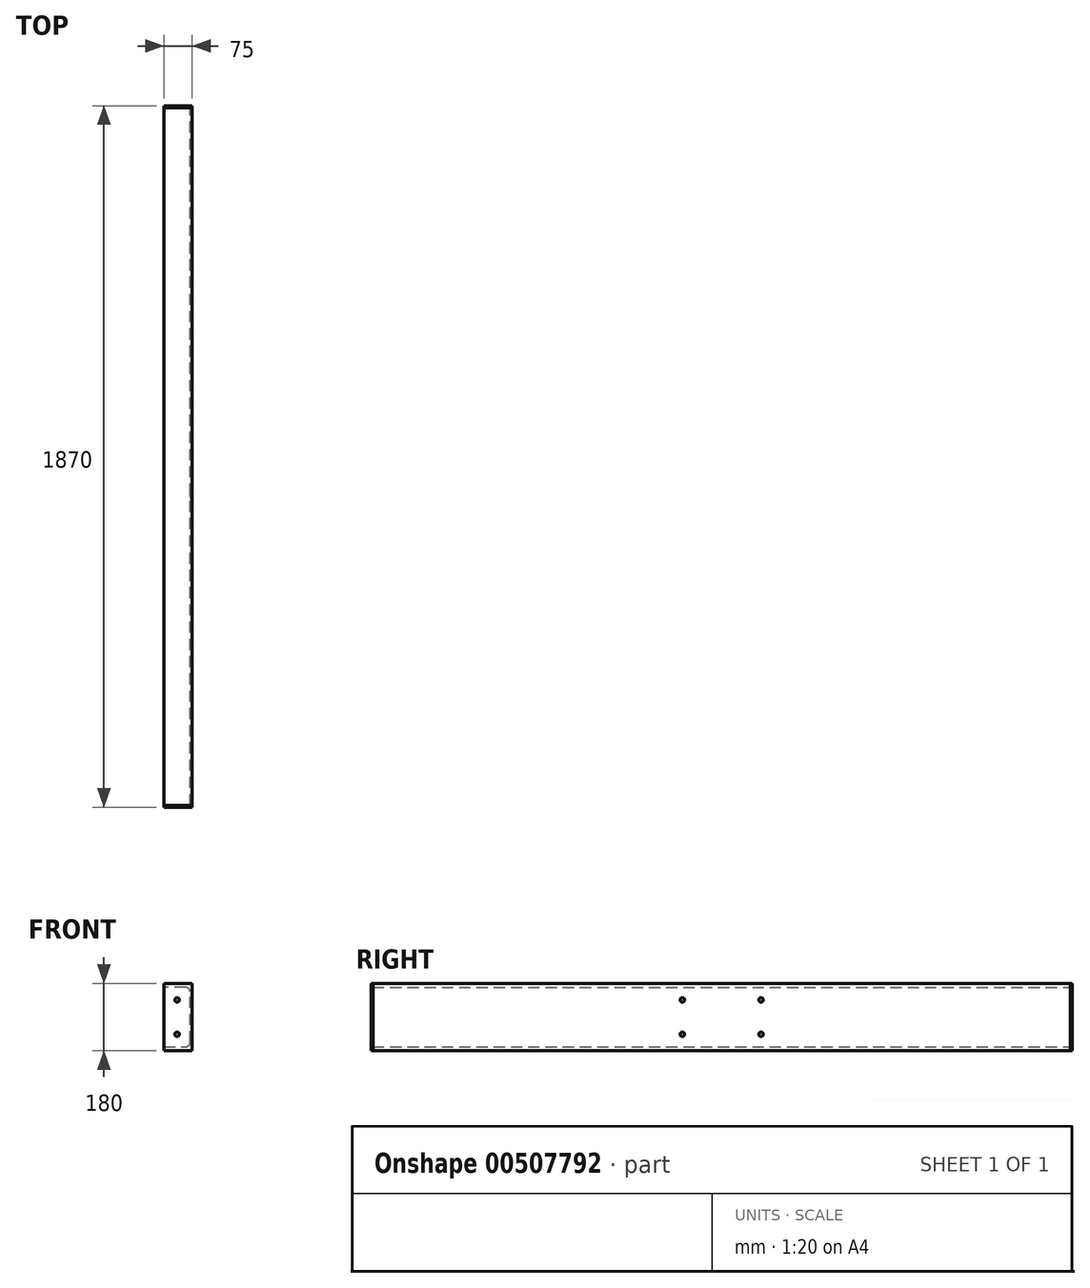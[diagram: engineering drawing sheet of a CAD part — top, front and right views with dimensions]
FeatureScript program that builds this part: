
annotation { "Feature Type Name" : "Feature", "Feature Type Description" : "" }
export const myFeature = defineFeature(function(context is Context, id is Id, definition is map)
    precondition{}
    {
        {
            var Q0;
            Q0=qCreatedBy(makeId("Front.planeOp"),FACE);
            var sketch = newSketch(context, id + "F0", { "sketchPlane" : qUnion([Q0])});
            skLineSegment(sketch, "E0", {"start": v(-69.5, 61.73) * mm, "end": v(5.5, 61.73) * mm});
            skLineSegment(sketch, "E1", {"start": v(5.5, 61.73) * mm, "end": v(5.5, -118.27) * mm});
            skLineSegment(sketch, "E2", {"start": v(5.5, -118.27) * mm, "end": v(-69.5, -118.27) * mm});
            skLineSegment(sketch, "E3", {"start": v(-69.5, -118.27) * mm, "end": v(-69.5, -107.77) * mm});
            skLineSegment(sketch, "E4", {"start": v(-69.5, -107.77) * mm, "end": v(-12, -107.77) * mm});
            skLineSegment(sketch, "E5", {"start": v(0, -95.77) * mm, "end": v(0, 39.23) * mm});
            skLineSegment(sketch, "E6", {"start": v(-12, 51.23) * mm, "end": v(-69.5, 51.23) * mm});
            skLineSegment(sketch, "E7", {"start": v(-69.5, 51.23) * mm, "end": v(-69.5, 61.73) * mm});
            skPoint(sketch, "E8.visualSharp", {"position": v(0, 51.23) * mm});
            skArc(sketch, "E8.filletArc", {"start": v(0, 39.23) * mm, "mid": v(-3.51, 47.71) * mm, "end": v(-12, 51.23) * mm});
            skPoint(sketch, "E9.visualSharp", {"position": v(0, -107.77) * mm});
            skArc(sketch, "E9.filletArc", {"start": v(-12, -107.77) * mm, "mid": v(-3.51, -104.26) * mm, "end": v(0, -95.77) * mm});
            skSolve(sketch);
        }
        {
            var Q0;
            Q0=makeQuery(id+"F0.imprint","IMPRINT",FACE,{"disambiguationData":[TD([[makeQuery(id+"F0.imprint","IMPRINT",EDGE,{"derivedFrom":sQuery(id+"F0.wireOp",EDGE,"E0")}),-1.0]])]});
            extrude(context, id + "F1", {"entities" : qUnion([Q0]), "endBound" : BoundingType.SYMMETRIC, "depth" : 1860 * mm});
        }
        {
            var Q0;
            Q0=makeQuery(id+"F1.opExtrude","SWEPT_FACE",FACE,{"disambiguationData":[OSD([sQuery(id+"F0.wireOp",EDGE,"E1")])]});
            var sketch = newSketch(context, id + "F2", { "sketchPlane" : qUnion([Q0])});
            skLineSegment(sketch, "E10.bottom", {"start": v(-930, 61.73) * mm, "end": v(-935, 61.73) * mm});
            skLineSegment(sketch, "E10.top", {"start": v(-930, -118.27) * mm, "end": v(-935, -118.27) * mm});
            skLineSegment(sketch, "E10.left", {"start": v(-930, 61.73) * mm, "end": v(-930, -118.27) * mm});
            skLineSegment(sketch, "E10.right", {"start": v(-935, 61.73) * mm, "end": v(-935, -118.27) * mm});
            skLineSegment(sketch, "E11.bottom", {"start": v(930, 61.73) * mm, "end": v(935, 61.73) * mm});
            skLineSegment(sketch, "E11.top", {"start": v(930, -118.27) * mm, "end": v(935, -118.27) * mm});
            skLineSegment(sketch, "E11.left", {"start": v(930, 61.73) * mm, "end": v(930, -118.27) * mm});
            skLineSegment(sketch, "E11.right", {"start": v(935, 61.73) * mm, "end": v(935, -118.27) * mm});
            skSolve(sketch);
        }
        {
            var Q0;
            Q0=makeQuery(id+"F2.imprint","IMPRINT",FACE,{"disambiguationData":[TD([[makeQuery(id+"F2.imprint","IMPRINT",EDGE,{"derivedFrom":sQuery(id+"F2.wireOp",EDGE,"E11.bottom")}),-1.0]])]});
            var Q1;
            Q1=makeQuery(id+"F2.imprint","IMPRINT",FACE,{"disambiguationData":[TD([[makeQuery(id+"F2.imprint","IMPRINT",EDGE,{"derivedFrom":sQuery(id+"F2.wireOp",EDGE,"E10.bottom")}),1.0]])]});
            extrude(context, id + "F3", {"entities" : qUnion([Q0, Q1]), "oppositeDirection" : true, "depth" : 75 * mm});
        }
        {
            var Q0;
            Q0=makeQuery(id+"F3.opExtrude","SWEPT_FACE",FACE,{"disambiguationData":[OSD([sQuery(id+"F2.wireOp",EDGE,"E10.right")])]});
            var sketch = newSketch(context, id + "F4", { "sketchPlane" : qUnion([Q0])});
            skCircle(sketch, "E12", {"center": v(-34.5, 17.73) * mm, "radius": 6 * mm});
            skCircle(sketch, "E13", {"center": v(-34.5, -74.27) * mm, "radius": 6 * mm});
            skSolve(sketch);
        }
        {
            var Q0;
            Q0=sQuery(id+"F4.wireOp",VERTEX,"E12.center");
            var Q1;
            Q1=sQuery(id+"F4.wireOp",VERTEX,"E13.center");
            var Q2;
            Q2=makeQuery(id+"F3.opExtrude","SWEPT_BODY",BODY,{"disambiguationData":[OSD([sQuery(id+"F2.wireOp",EDGE,"E10.bottom"),sQuery(id+"F2.wireOp",EDGE,"E10.top"),sQuery(id+"F2.wireOp",EDGE,"E10.left"),sQuery(id+"F2.wireOp",EDGE,"E10.right")])]});
            var Q3;
            Q3=makeQuery(id+"F3.opExtrude","SWEPT_BODY",BODY,{"disambiguationData":[OSD([sQuery(id+"F2.wireOp",EDGE,"E11.bottom"),sQuery(id+"F2.wireOp",EDGE,"E11.top"),sQuery(id+"F2.wireOp",EDGE,"E11.left"),sQuery(id+"F2.wireOp",EDGE,"E11.right")])]});
            hole(context, id + "F5", {"style" : HoleStyle.SIMPLE, "endStyle" : HoleEndStyle.THROUGH, "holeDiameter" : 12 * mm, "isTappedThrough" : true, "tappedDepth" : 12 * mm, "tapClearance" : 3, "locations" : qUnion([Q0, Q1]), "scope" : qUnion([Q2, Q3])});
        }
        {
            var Q0;
            Q0=makeQuery(id+"F1.opExtrude","SWEPT_FACE",FACE,{"disambiguationData":[OSD([sQuery(id+"F0.wireOp",EDGE,"E1")])]});
            var sketch = newSketch(context, id + "F6", { "sketchPlane" : qUnion([Q0])});
            skCircle(sketch, "E14", {"center": v(-105, 17.73) * mm, "radius": 6 * mm});
            skCircle(sketch, "E15", {"center": v(-105, -74.27) * mm, "radius": 6 * mm});
            skCircle(sketch, "E16.MirrorC", {"center": v(105, 17.73) * mm, "radius": 6 * mm});
            skCircle(sketch, "E17.MirrorC", {"center": v(105, -74.27) * mm, "radius": 6 * mm});
            skSolve(sketch);
        }
        {
            var Q0;
            Q0=sQuery(id+"F6.wireOp",VERTEX,"E14.center");
            var Q1;
            Q1=sQuery(id+"F6.wireOp",VERTEX,"E16.MirrorC.center");
            var Q2;
            Q2=sQuery(id+"F6.wireOp",VERTEX,"E17.MirrorC.center");
            var Q3;
            Q3=sQuery(id+"F6.wireOp",VERTEX,"E15.center");
            var Q4;
            Q4=makeQuery(id+"F1.opExtrude","SWEPT_BODY",BODY,{"disambiguationData":[OSD([sQuery(id+"F0.wireOp",EDGE,"E0"),sQuery(id+"F0.wireOp",EDGE,"E1"),sQuery(id+"F0.wireOp",EDGE,"E2"),sQuery(id+"F0.wireOp",EDGE,"E3"),sQuery(id+"F0.wireOp",EDGE,"E4"),sQuery(id+"F0.wireOp",EDGE,"E5"),sQuery(id+"F0.wireOp",EDGE,"E6"),sQuery(id+"F0.wireOp",EDGE,"E7"),sQuery(id+"F0.wireOp",EDGE,"E8.filletArc"),sQuery(id+"F0.wireOp",EDGE,"E9.filletArc")])]});
            hole(context, id + "F7", {"style" : HoleStyle.SIMPLE, "endStyle" : HoleEndStyle.THROUGH, "holeDiameter" : 12 * mm, "isTappedThrough" : true, "tappedDepth" : 12 * mm, "tapClearance" : 3, "locations" : qUnion([Q0, Q1, Q2, Q3]), "scope" : qUnion([Q4])});
        }
    });
